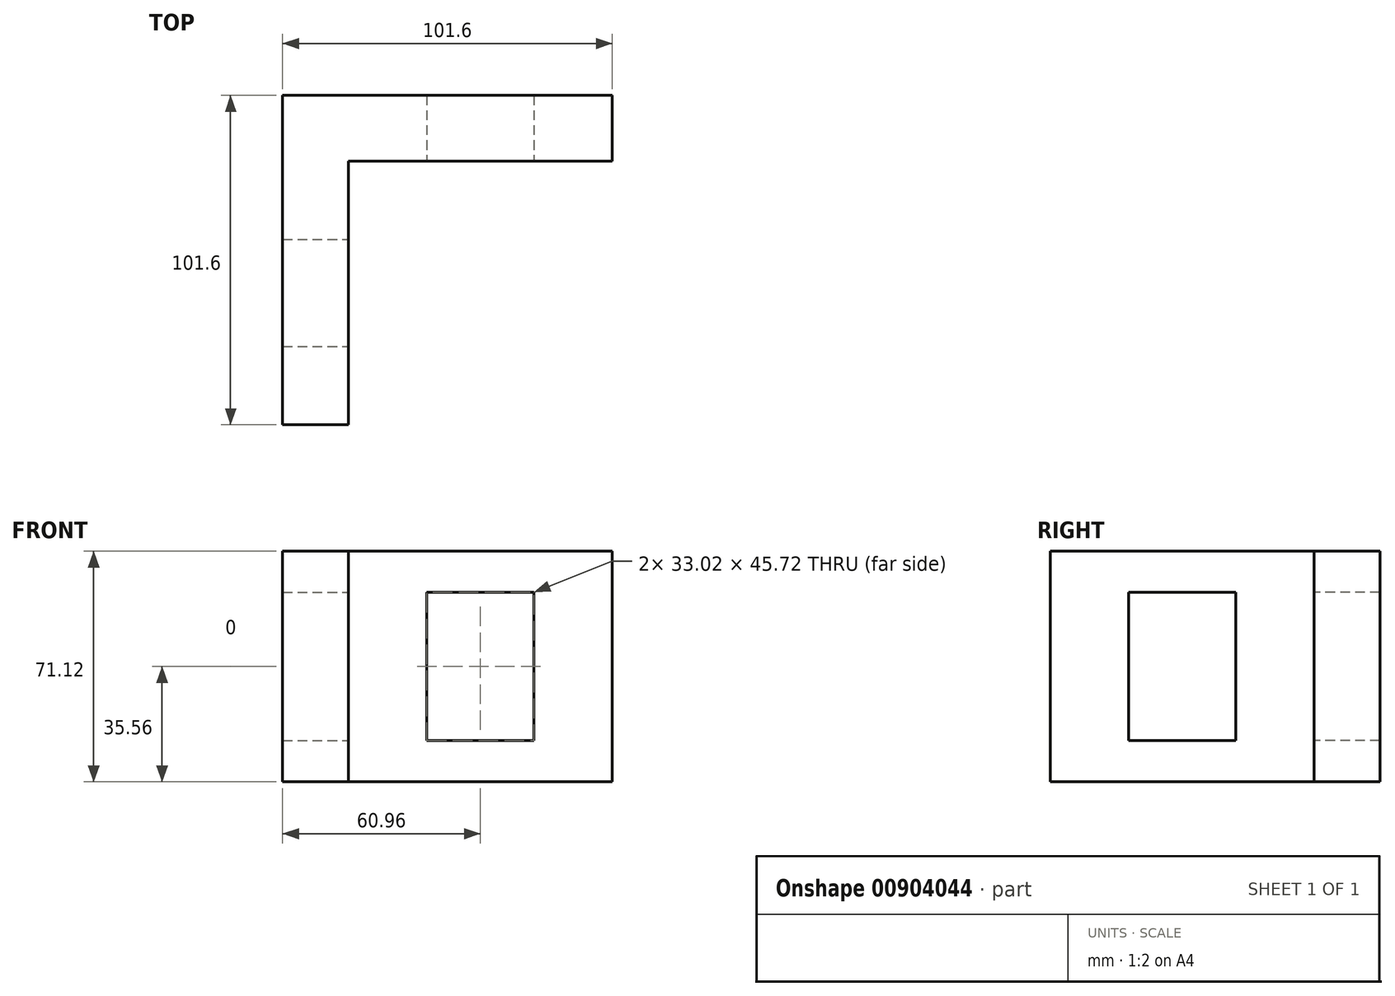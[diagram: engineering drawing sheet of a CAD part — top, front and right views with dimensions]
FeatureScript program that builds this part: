
annotation { "Feature Type Name" : "Feature", "Feature Type Description" : "" }
export const myFeature = defineFeature(function(context is Context, id is Id, definition is map)
    precondition{}
    {
        {
            var Q0;
            Q0=qCreatedBy(makeId("Front.planeOp"),FACE);
            var sketch = newSketch(context, id + "F0", { "sketchPlane" : qUnion([Q0])});
            skLineSegment(sketch, "E0.bottom", {"start": v(50.8, 35.56) * mm, "end": v(-50.8, 35.56) * mm});
            skLineSegment(sketch, "E0.top", {"start": v(50.8, -35.56) * mm, "end": v(-50.8, -35.56) * mm});
            skLineSegment(sketch, "E0.left", {"start": v(50.8, 35.56) * mm, "end": v(50.8, -35.56) * mm});
            skLineSegment(sketch, "E0.right", {"start": v(-50.8, 35.56) * mm, "end": v(-50.8, -35.56) * mm});
            skPoint(sketch, "E0.middle", {"position": v(0, 0) * mm});
            skSolve(sketch);
        }
        {
            var Q0;
            Q0=makeQuery(id+"F0.imprint","IMPRINT",FACE,{"disambiguationData":[TD([[makeQuery(id+"F0.imprint","IMPRINT",EDGE,{"derivedFrom":sQuery(id+"F0.wireOp",EDGE,"E0.bottom")}),1.0]])]});
            extrude(context, id + "F1", {"entities" : qUnion([Q0]), "depth" : 101.6 * mm, "offsetDistance" : 25.4 * mm});
        }
        {
            var Q0;
            Q0=makeQuery(id+"F1.opExtrude","CAP_FACE",FACE,{"disambiguationData":[OSD([sQuery(id+"F0.wireOp",EDGE,"E0.bottom"),sQuery(id+"F0.wireOp",EDGE,"E0.top"),sQuery(id+"F0.wireOp",EDGE,"E0.left"),sQuery(id+"F0.wireOp",EDGE,"E0.right")])],"isStart":false});
            var sketch = newSketch(context, id + "F2", { "sketchPlane" : qUnion([Q0])});
            skLineSegment(sketch, "E1.bottom", {"start": v(50.8, 35.56) * mm, "end": v(-30.48, 35.56) * mm});
            skLineSegment(sketch, "E1.top", {"start": v(50.8, -35.56) * mm, "end": v(-30.48, -35.56) * mm});
            skLineSegment(sketch, "E1.left", {"start": v(50.8, 35.56) * mm, "end": v(50.8, -35.56) * mm});
            skLineSegment(sketch, "E1.right", {"start": v(-30.48, 35.56) * mm, "end": v(-30.48, -35.56) * mm});
            skSolve(sketch);
        }
        {
            var Q0;
            Q0=makeQuery(id+"F2.imprint","IMPRINT",FACE,{"disambiguationData":[TD([[makeQuery(id+"F2.imprint","IMPRINT",EDGE,{"derivedFrom":sQuery(id+"F2.wireOp",EDGE,"E1.bottom")}),1.0]])]});
            extrude(context, id + "F3", {"entities" : qUnion([Q0]), "operationType" : NewBodyOperationType.REMOVE, "oppositeDirection" : true, "depth" : 81.28 * mm, "offsetDistance" : 25.4 * mm});
        }
        {
            var Q0;
            Q0=makeQuery(id+"F3.boolean.opBoolean","COPY",FACE,{"derivedFrom":makeQuery(id+"F3.opExtrude","CAP_FACE",FACE,{"disambiguationData":[OSD([sQuery(id+"F2.wireOp",EDGE,"E1.bottom"),sQuery(id+"F2.wireOp",EDGE,"E1.top"),sQuery(id+"F2.wireOp",EDGE,"E1.left"),sQuery(id+"F2.wireOp",EDGE,"E1.right")])],"isStart":false})});
            var sketch = newSketch(context, id + "F4", { "sketchPlane" : qUnion([Q0])});
            skLineSegment(sketch, "E2.bottom", {"start": v(26.67, -22.86) * mm, "end": v(-6.35, -22.86) * mm});
            skLineSegment(sketch, "E2.top", {"start": v(26.67, 22.86) * mm, "end": v(-6.35, 22.86) * mm});
            skLineSegment(sketch, "E2.left", {"start": v(26.67, -22.86) * mm, "end": v(26.67, 22.86) * mm});
            skLineSegment(sketch, "E2.right", {"start": v(-6.35, -22.86) * mm, "end": v(-6.35, 22.86) * mm});
            skPoint(sketch, "E2.middle", {"position": v(10.16, 0) * mm});
            skSolve(sketch);
        }
        {
            var Q0;
            Q0=makeQuery(id+"F4.imprint","IMPRINT",FACE,{"disambiguationData":[TD([[makeQuery(id+"F4.imprint","IMPRINT",EDGE,{"derivedFrom":sQuery(id+"F4.wireOp",EDGE,"E2.bottom")}),-1.0]])]});
            extrude(context, id + "F5", {"entities" : qUnion([Q0]), "operationType" : NewBodyOperationType.REMOVE, "endBound" : BoundingType.THROUGH_ALL, "oppositeDirection" : true, "depth" : 25.4 * mm, "offsetDistance" : 25.4 * mm});
        }
        {
            var Q0;
            Q0=makeQuery(id+"F3.boolean.opBoolean","COPY",FACE,{"derivedFrom":makeQuery(id+"F3.opExtrude","SWEPT_FACE",FACE,{"disambiguationData":[OSD([sQuery(id+"F2.wireOp",EDGE,"E1.right")])]})});
            var sketch = newSketch(context, id + "F6", { "sketchPlane" : qUnion([Q0])});
            skLineSegment(sketch, "E3.bottom", {"start": v(-77.47, 22.86) * mm, "end": v(-44.45, 22.86) * mm});
            skLineSegment(sketch, "E3.top", {"start": v(-77.47, -22.86) * mm, "end": v(-44.45, -22.86) * mm});
            skLineSegment(sketch, "E3.left", {"start": v(-77.47, 22.86) * mm, "end": v(-77.47, -22.86) * mm});
            skLineSegment(sketch, "E3.right", {"start": v(-44.45, 22.86) * mm, "end": v(-44.45, -22.86) * mm});
            skPoint(sketch, "E3.middle", {"position": v(-60.96, 0) * mm});
            skSolve(sketch);
        }
        {
            var Q0;
            Q0=makeQuery(id+"F6.imprint","IMPRINT",FACE,{"disambiguationData":[TD([[makeQuery(id+"F6.imprint","IMPRINT",EDGE,{"derivedFrom":sQuery(id+"F6.wireOp",EDGE,"E3.bottom")}),-1.0]])]});
            extrude(context, id + "F7", {"entities" : qUnion([Q0]), "operationType" : NewBodyOperationType.REMOVE, "endBound" : BoundingType.THROUGH_ALL, "oppositeDirection" : true, "depth" : 25.4 * mm, "offsetDistance" : 25.4 * mm});
        }
    });
